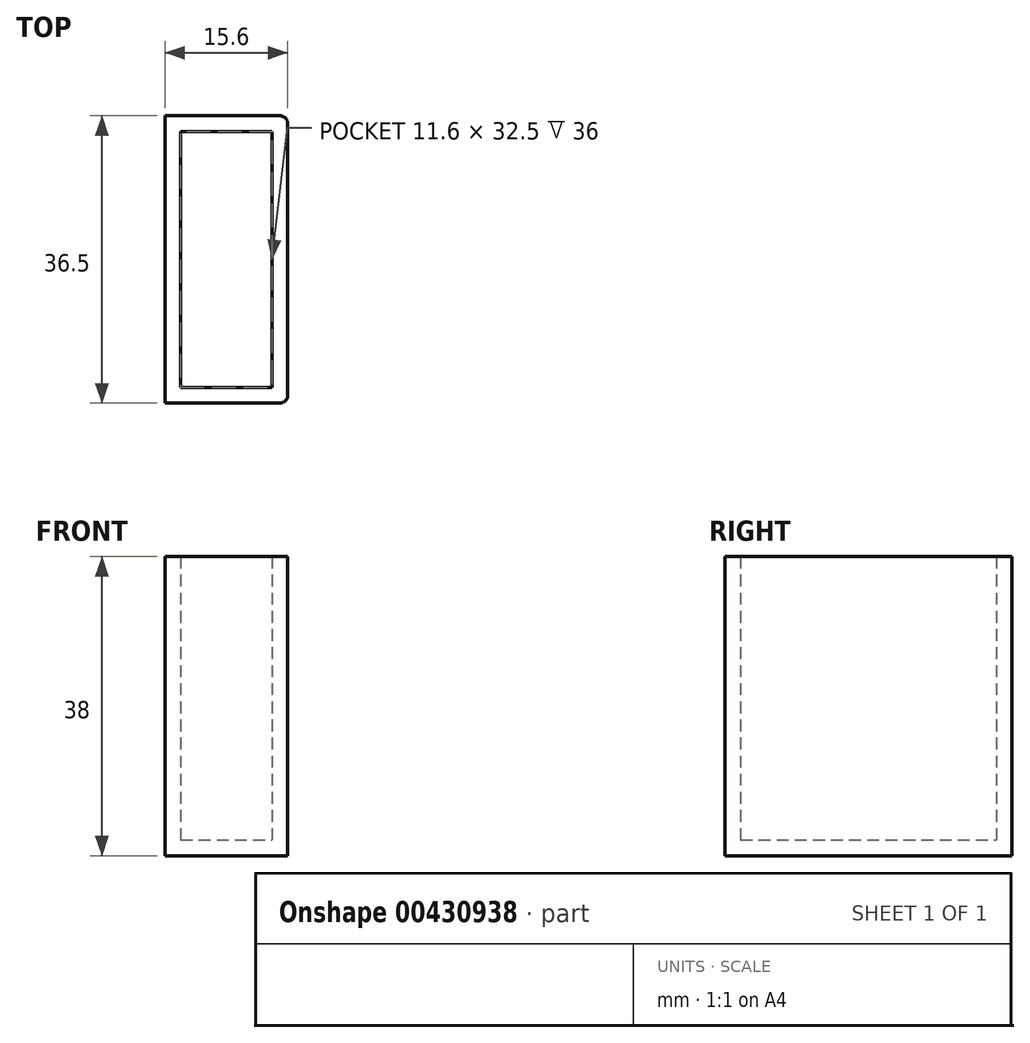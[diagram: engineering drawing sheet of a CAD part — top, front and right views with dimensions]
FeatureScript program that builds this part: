
annotation { "Feature Type Name" : "Feature", "Feature Type Description" : "" }
export const myFeature = defineFeature(function(context is Context, id is Id, definition is map)
    precondition{}
    {
        {
            var Q0;
            Q0=qCreatedBy(makeId("Top.planeOp"),FACE);
            var sketch = newSketch(context, id + "F0", { "sketchPlane" : qUnion([Q0])});
            skLineSegment(sketch, "E0.bottom", {"start": v(0, 0) * mm, "end": v(15.6, 0) * mm});
            skLineSegment(sketch, "E0.top", {"start": v(0, 36.5) * mm, "end": v(15.6, 36.5) * mm});
            skLineSegment(sketch, "E0.left", {"start": v(0, 0) * mm, "end": v(0, 36.5) * mm});
            skLineSegment(sketch, "E0.right", {"start": v(15.6, 0) * mm, "end": v(15.6, 36.5) * mm});
            skSolve(sketch);
        }
        {
            var Q0;
            Q0=qSketchRegion(id+"F0",true);
            extrude(context, id + "F1", {"entities" : qUnion([Q0]), "depth" : 38 * mm});
        }
        {
            var Q0;
            Q0=makeQuery(id+"F1.opExtrude","CAP_FACE",FACE,{"disambiguationData":[OSD([sQuery(id+"F0.wireOp",EDGE,"E0.bottom"),sQuery(id+"F0.wireOp",EDGE,"E0.top"),sQuery(id+"F0.wireOp",EDGE,"E0.left"),sQuery(id+"F0.wireOp",EDGE,"E0.right")])],"isStart":false});
            shell(context, id + "F2", {"entities" : qUnion([Q0]), "thickness" : 2 * mm});
        }
        {
            var Q0;
            Q0=makeQuery(id+"F1.opExtrude","SWEPT_EDGE",EDGE,{"disambiguationData":[OSD([sQuery(id+"F0.wireOp",EDGE,"E0.bottom"),sQuery(id+"F0.wireOp",EDGE,"E0.right")])]});
            var Q1;
            Q1=makeQuery(id+"F1.opExtrude","SWEPT_EDGE",EDGE,{"disambiguationData":[OSD([sQuery(id+"F0.wireOp",EDGE,"E0.top"),sQuery(id+"F0.wireOp",EDGE,"E0.right")])]});
            fillet(context, id + "F3", {"entities" : qUnion([Q0, Q1]), "radius" : 1 * mm, "tangentPropagation" : true, "allowEdgeOverflow" : false});
        }
    });
